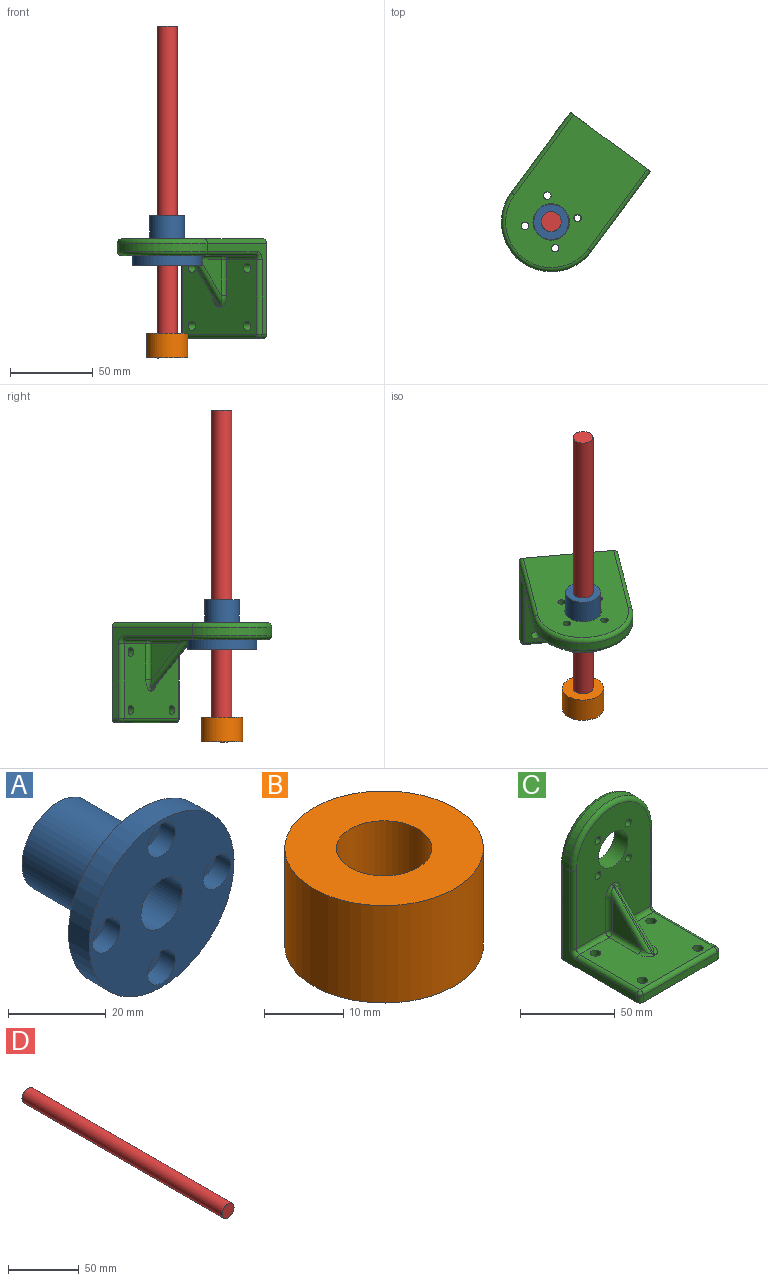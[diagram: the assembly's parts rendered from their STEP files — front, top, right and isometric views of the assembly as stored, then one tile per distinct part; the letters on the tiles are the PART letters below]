
ASSEMBLY  parts=4 mates=4
PART A: 18 faces, bbox 42x30x42 mm
  f0: cylinder r=2.25mm len=4.5mm, axis (0,-1,0), area 22.6mm2, adj f7,f14
  f1: cylinder r=2mm len=4mm, axis (0,-1,0), area 20.1mm2, adj f7,f12
  f2: cylinder r=2.25mm len=4.5mm, axis (0,-1,0), area 22.6mm2, adj f7,f10
  f3: cylinder r=2.25mm len=4.5mm, axis (0,-1,0), area 22.6mm2, adj f7,f8
  f4: cylinder r=6mm len=30mm, axis (0,1,0), area 1131mm2, adj f6,f17
  f5: cylinder r=21mm len=42mm, axis (0,1,0), area 791.7mm2, adj f6,f7
  f6: plane 42x42mm, normal (0,-1,0), area 1071.3mm2, adj f4,f5,f9,f11,f13,f15
  f7: plane 42x42mm, normal (0,1,0), area 978.8mm2, adj f0,f1,f2,f3,f5,f16
  f8: plane 8x8mm, normal (0,-1,0), area 34.4mm2, adj f3,f9
  f9: cylinder r=4mm len=8mm, axis (0,-1,0), area 110.6mm2, adj f6,f8
  f10: plane 8x8mm, normal (0,-1,0), area 34.4mm2, adj f2,f11
  f11: cylinder r=4mm len=8mm, axis (0,-1,0), area 110.6mm2, adj f6,f10
  f12: plane 8x8mm, normal (0,-1,0), area 37.7mm2, adj f1,f13
  f13: cylinder r=4mm len=8mm, axis (0,-1,0), area 110.6mm2, adj f6,f12
  f14: plane 8x8mm, normal (0,-1,0), area 34.4mm2, adj f0,f15
  f15: cylinder r=4mm len=8mm, axis (0,-1,0), area 110.6mm2, adj f6,f14
  f16: cylinder r=10.5mm len=24mm, axis (0,-1,0), area 1583.4mm2, adj f7,f17
  f17: plane 21x21mm, normal (0,1,0), area 233.3mm2, adj f4,f16
PART B: 4 faces, bbox 25x25x15 mm
  f0: cylinder r=6mm len=15mm, axis (0,0,-1), area 565.5mm2, adj f2,f3
  f1: cylinder r=12.5mm len=25mm, axis (0,0,-1), area 1178.1mm2, adj f2,f3
  f2: plane 25x25mm, normal (0,0,1), area 377.8mm2, adj f0,f1
  f3: plane 25x25mm, normal (0,0,-1), area 377.8mm2, adj f0,f1
PART C: 51 faces, bbox 64.9x60x92.5 mm
  f0: plane 78x55mm, normal (0,-1,0), area 3222.9mm2, adj f5,f6,f7,f8,f9,f21,f24,f28
  f1: plane 55x45mm, normal (0,0,1), area 2081.3mm2, adj f13,f14,f15,f16,f22,f23,f26,f29
  f2: plane 60x60mm, normal (0,0,-1), area 3499.6mm2, adj f3,f4,f11,f12,f13,f14,f15,f16
  f3: plane 60x55mm, normal (-1,0,0), area 530.4mm2, adj f2,f10,f32,f33,f34,f37,f50
  f4: plane 60x55mm, normal (1,0,0), area 530.4mm2, adj f2,f10,f41,f44,f46,f47,f48
  f5: cylinder r=11mm len=22mm, axis (0,1,0), area 691.2mm2, adj f0,f11
  f6: cylinder r=2.25mm len=10mm, axis (0,1,0), area 141.4mm2, adj f0,f11
  f7: cylinder r=2.25mm len=10mm, axis (0,1,0), area 141.4mm2, adj f0,f11
  f8: cylinder r=2.25mm len=10mm, axis (0,1,0), area 141.4mm2, adj f0,f11
  f9: cylinder r=2.25mm len=10mm, axis (0,1,0), area 141.4mm2, adj f0,f11
  f10: cylinder r=30mm len=60mm, axis (0,1,0), area 471.2mm2, adj f3,f4,f40,f49
  f11: plane 87.5x55mm, normal (0,1,0), area 4044.2mm2, adj f2,f5,f6,f7,f8,f9,f48,f49
  f12: plane 55x4.5mm, normal (0,-1,0), area 247.5mm2, adj f2,f33,f41,f42
  f13: cylinder r=2.75mm len=7mm, axis (0,0,1), area 121mm2, adj f1,f2
  f14: cylinder r=2.75mm len=7mm, axis (0,0,1), area 121mm2, adj f1,f2
  f15: cylinder r=2.75mm len=7mm, axis (0,0,1), area 121mm2, adj f1,f2
  f16: cylinder r=2.75mm len=7mm, axis (0,0,1), area 121mm2, adj f1,f2
  f17: plane 28.54x28.54mm, normal (0,-0.71,0.71), area 40.4mm2, adj f20,f26,f27,f28
  f18: plane 21.46x21.46mm, normal (1,0,0), area 230.4mm2, adj f27,f35,f36
  f19: plane 21.46x21.46mm, normal (-1,0,0), area 230.4mm2, adj f20,f21,f22
  f20: cylinder r=2.5mm len=30.3mm, axis (0,-0.71,-0.71), area 144.2mm2, adj f17,f19,f23,f24
  f21: cylinder r=2.5mm len=21.46mm, axis (0,0,-1), area 84.3mm2, adj f0,f19,f24,f25
  f22: cylinder r=2.5mm len=21.46mm, axis (0,1,0), area 84.3mm2, adj f1,f19,f23,f25
  f23: bspline ~7.07x5mm, area 21.8mm2, adj f1,f20,f22,f26
  f24: bspline ~8.3x5.87mm, area 21.8mm2, adj f0,f20,f21,f28
  f25: sphere r=2.5mm, area 9.8mm2, adj f21,f22,f29
  f26: cylinder r=2.5mm len=1.77mm, axis (1,0,0), area 2mm2, adj f1,f17,f23,f30
  f27: cylinder r=2.5mm len=30.3mm, axis (0,0.71,0.71), area 144.2mm2, adj f17,f18,f30,f31
  f28: cylinder r=2.5mm len=1.77mm, axis (1,0,0), area 2mm2, adj f0,f17,f24,f31
  f29: cylinder r=2.5mm len=22mm, axis (-1,0,0), area 86.4mm2, adj f0,f1,f25,f32
  f30: bspline ~7.07x5mm, area 21.8mm2, adj f1,f26,f27,f35
  f31: bspline ~7.07x5mm, area 21.8mm2, adj f0,f27,f28,f36
  f32: torus R=5mm, axis (1,0,0), area 21mm2, adj f3,f29,f34,f37
  f33: cylinder r=2.5mm len=4.5mm, axis (0,0,1), area 17.7mm2, adj f2,f3,f12,f38
  f34: cylinder r=2.5mm len=45mm, axis (0,-1,0), area 176.7mm2, adj f1,f3,f32,f38
  f35: cylinder r=2.5mm len=21.46mm, axis (0,-1,0), area 84.3mm2, adj f1,f18,f30,f39
  f36: cylinder r=2.5mm len=21.46mm, axis (0,0,1), area 84.3mm2, adj f0,f18,f31,f39
  f37: cylinder r=2.5mm len=50.5mm, axis (0,0,1), area 198.3mm2, adj f0,f3,f32,f40
  f38: sphere r=2.5mm, area 9.8mm2, adj f33,f34,f42
  f39: sphere r=2.5mm, area 9.8mm2, adj f35,f36,f43
  f40: torus R=27.5mm, axis (0,-1,0), area 358.9mm2, adj f0,f10,f37,f44
  f41: cylinder r=2.5mm len=4.5mm, axis (0,0,-1), area 17.7mm2, adj f2,f4,f12,f45
  f42: cylinder r=2.5mm len=55mm, axis (1,0,0), area 216mm2, adj f1,f12,f38,f45
  f43: cylinder r=2.5mm len=22mm, axis (-1,0,0), area 86.4mm2, adj f0,f1,f39,f46
  f44: cylinder r=2.5mm len=50.5mm, axis (0,0,-1), area 198.3mm2, adj f0,f4,f40,f46
  f45: sphere r=2.5mm, area 9.8mm2, adj f41,f42,f47
  f46: torus R=5mm, axis (1,0,0), area 21mm2, adj f4,f43,f44,f47
  f47: cylinder r=2.5mm len=45mm, axis (0,1,0), area 176.7mm2, adj f1,f4,f45,f46
  f48: cylinder r=2.5mm len=60mm, axis (0,0,1), area 235.6mm2, adj f2,f4,f11,f49
  f49: torus R=27.5mm, axis (0,-1,0), area 358.9mm2, adj f10,f11,f48,f50
  f50: cylinder r=2.5mm len=60mm, axis (0,0,-1), area 235.6mm2, adj f2,f3,f11,f49
PART D: 3 faces, bbox 12x200x12 mm
  f0: cylinder r=6mm len=200mm, axis (0,1,0), area 7539.8mm2, adj f1,f2
  f1: plane 12x12mm, normal (0,-1,0), area 113.1mm2, adj f0
  f2: plane 12x12mm, normal (0,1,0), area 113.1mm2, adj f0
PLACE A rot(axis=(0.63,-0.55,-0.55),115.2deg) t=(144.86,80.36,101.78)mm
PLACE B t=(144.86,80.36,40.03)mm
PLACE C rot(axis=(0.91,-0.3,-0.3),95.6deg) t=(144.86,80.36,111.78)mm
PLACE D rot(axis=(0.99,0.07,0.07),90.3deg) t=(144.86,80.36,240.03)mm
MATE parallel C.f0 <-> A.f7  axis (0,0,-1) through (153.22,91.65,101.78)mm
MATE cylindrical D.f0 <-> B.f0  axis (0,0,1) through (144.86,80.36,140.03)mm
MATE cylindrical C.f5 <-> A.f16  axis (0,0,1) through (144.86,80.36,101.78)mm
MATE cylindrical D.f0 <-> A.f4  axis (0,0,1) through (144.86,80.36,140.03)mm
